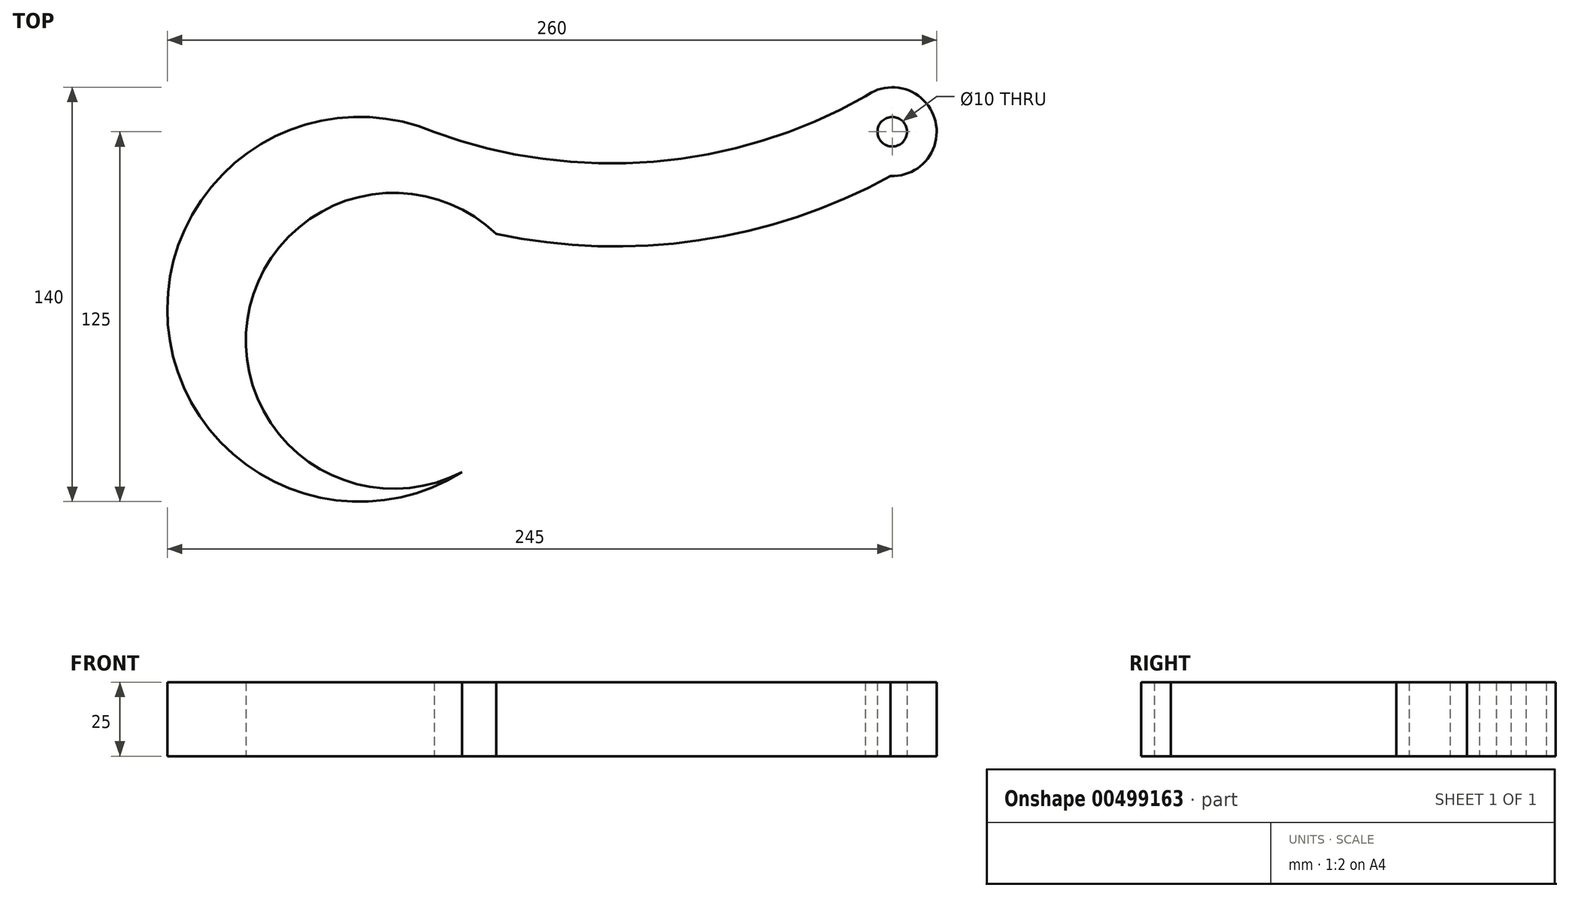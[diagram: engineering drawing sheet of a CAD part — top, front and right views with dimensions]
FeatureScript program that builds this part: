
annotation { "Feature Type Name" : "Feature", "Feature Type Description" : "" }
export const myFeature = defineFeature(function(context is Context, id is Id, definition is map)
    precondition{}
    {
        {
            var Q0;
            Q0=qCreatedBy(makeId("Top.planeOp"),FACE);
            var sketch = newSketch(context, id + "F0", { "sketchPlane" : qUnion([Q0])});
            skArc(sketch, "E0", {"start": v(25.24, 59.9) * mm, "mid": v(-64.79, -5.27) * mm, "end": v(34.6, -55.03) * mm});
            skPoint(sketch, "E1", {"position": v(180, 60) * mm});
            skArc(sketch, "E2", {"start": v(179.45, 45.01) * mm, "mid": v(194.3, 64.56) * mm, "end": v(170.87, 71.9) * mm});
            skArc(sketch, "E3", {"start": v(25.24, 59.9) * mm, "mid": v(99.38, 49.88) * mm, "end": v(170.87, 71.9) * mm});
            skArc(sketch, "E4", {"start": v(46.18, 25.45) * mm, "mid": v(-37.91, -3.52) * mm, "end": v(34.6, -55.03) * mm});
            skArc(sketch, "E5", {"start": v(46.18, 25.45) * mm, "mid": v(114.57, 23.29) * mm, "end": v(179.45, 45.01) * mm});
            skCircle(sketch, "E6", {"center": v(180, 60) * mm, "radius": 5 * mm});
            skSolve(sketch);
        }
        {
            var Q0;
            Q0 = qSketchRegion(id + "F0", true);
            extrude(context, id + "F1", {"entities" : qUnion([Q0]), "depth" : 25 * mm});
        }
    });
